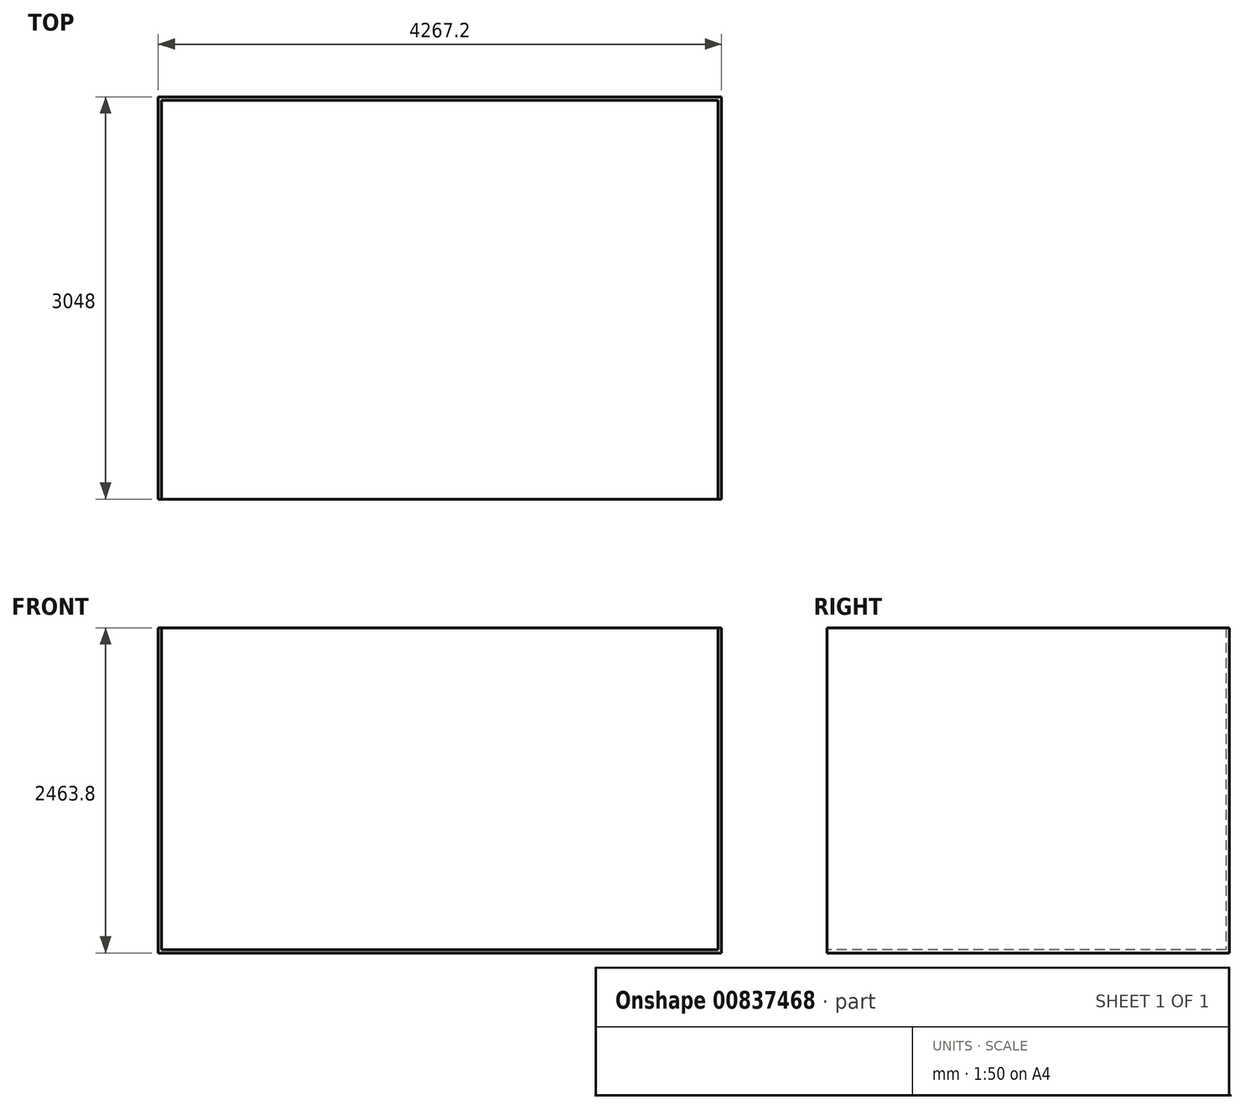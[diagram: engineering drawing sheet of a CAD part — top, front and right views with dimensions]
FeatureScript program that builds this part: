
annotation { "Feature Type Name" : "Feature", "Feature Type Description" : "" }
export const myFeature = defineFeature(function(context is Context, id is Id, definition is map)
    precondition{}
    {
        {
            var Q0;
            Q0=qCreatedBy(makeId("Top.planeOp"),FACE);
            var sketch = newSketch(context, id + "F0", { "sketchPlane" : qUnion([Q0])});
            skLineSegment(sketch, "E0.bottom", {"start": v(0, 0) * mm, "end": v(4267.2, 0) * mm});
            skLineSegment(sketch, "E0.top", {"start": v(0, -3048) * mm, "end": v(4267.2, -3048) * mm});
            skLineSegment(sketch, "E0.left", {"start": v(0, 0) * mm, "end": v(0, -3048) * mm});
            skLineSegment(sketch, "E0.right", {"start": v(4267.2, 0) * mm, "end": v(4267.2, -3048) * mm});
            skSolve(sketch);
        }
        {
            var Q0;
            Q0 = qSketchRegion(id + "F0", true);
            extrude(context, id + "F1", {"entities" : qUnion([Q0]), "depth" : 25.4 * mm, "offsetDistance" : 25.4 * mm});
        }
        {
            var Q0;
            Q0=makeQuery(id+"F1.opExtrude","CAP_FACE",FACE,{"disambiguationData":[OSD([sQuery(id+"F0.wireOp",EDGE,"E0.bottom"),sQuery(id+"F0.wireOp",EDGE,"E0.top"),sQuery(id+"F0.wireOp",EDGE,"E0.left"),sQuery(id+"F0.wireOp",EDGE,"E0.right")])],"isStart":false});
            var sketch = newSketch(context, id + "F2", { "sketchPlane" : qUnion([Q0])});
            skSolve(sketch);
        }
        {
            var Q0;
            Q0=makeQuery(id+"F2.imprint","IMPRINT",FACE,{"disambiguationData":[TD([[makeQuery(id+"F2.imprint","IMPRINT",EDGE,{"derivedFrom":makeQuery(id+"F1.opExtrude","CAP_EDGE",EDGE,{"disambiguationData":[OSD([sQuery(id+"F0.wireOp",EDGE,"E0.bottom")])],"isStart":false})}),-1.0]])]});
            var sketch = newSketch(context, id + "F3", { "sketchPlane" : qUnion([Q0])});
            skLineSegment(sketch, "E1.bottom", {"start": v(0, 0) * mm, "end": v(4267.2, 0) * mm});
            skLineSegment(sketch, "E1.top", {"start": v(0, -25.4) * mm, "end": v(4267.2, -25.4) * mm});
            skLineSegment(sketch, "E1.left", {"start": v(0, 0) * mm, "end": v(0, -25.4) * mm});
            skLineSegment(sketch, "E1.right", {"start": v(4267.2, 0) * mm, "end": v(4267.2, -25.4) * mm});
            skLineSegment(sketch, "E2.bottom", {"start": v(25.4, -25.4) * mm, "end": v(0, -25.4) * mm});
            skLineSegment(sketch, "E2.top", {"start": v(25.4, -3048) * mm, "end": v(0, -3048) * mm});
            skLineSegment(sketch, "E2.left", {"start": v(25.4, -25.4) * mm, "end": v(25.4, -3048) * mm});
            skLineSegment(sketch, "E2.right", {"start": v(0, -25.4) * mm, "end": v(0, -3048) * mm});
            skLineSegment(sketch, "E3.bottom", {"start": v(4267.2, -25.4) * mm, "end": v(4241.8, -25.4) * mm});
            skLineSegment(sketch, "E3.top", {"start": v(4267.2, -3048) * mm, "end": v(4241.8, -3048) * mm});
            skLineSegment(sketch, "E3.left", {"start": v(4267.2, -25.4) * mm, "end": v(4267.2, -3048) * mm});
            skLineSegment(sketch, "E3.right", {"start": v(4241.8, -25.4) * mm, "end": v(4241.8, -3048) * mm});
            skSolve(sketch);
        }
        {
            var Q0;
            Q0 = qSketchRegion(id + "F3", true);
            extrude(context, id + "F4", {"entities" : qUnion([Q0]), "operationType" : NewBodyOperationType.ADD, "depth" : 2438.4 * mm, "offsetDistance" : 25.4 * mm});
        }
    });
